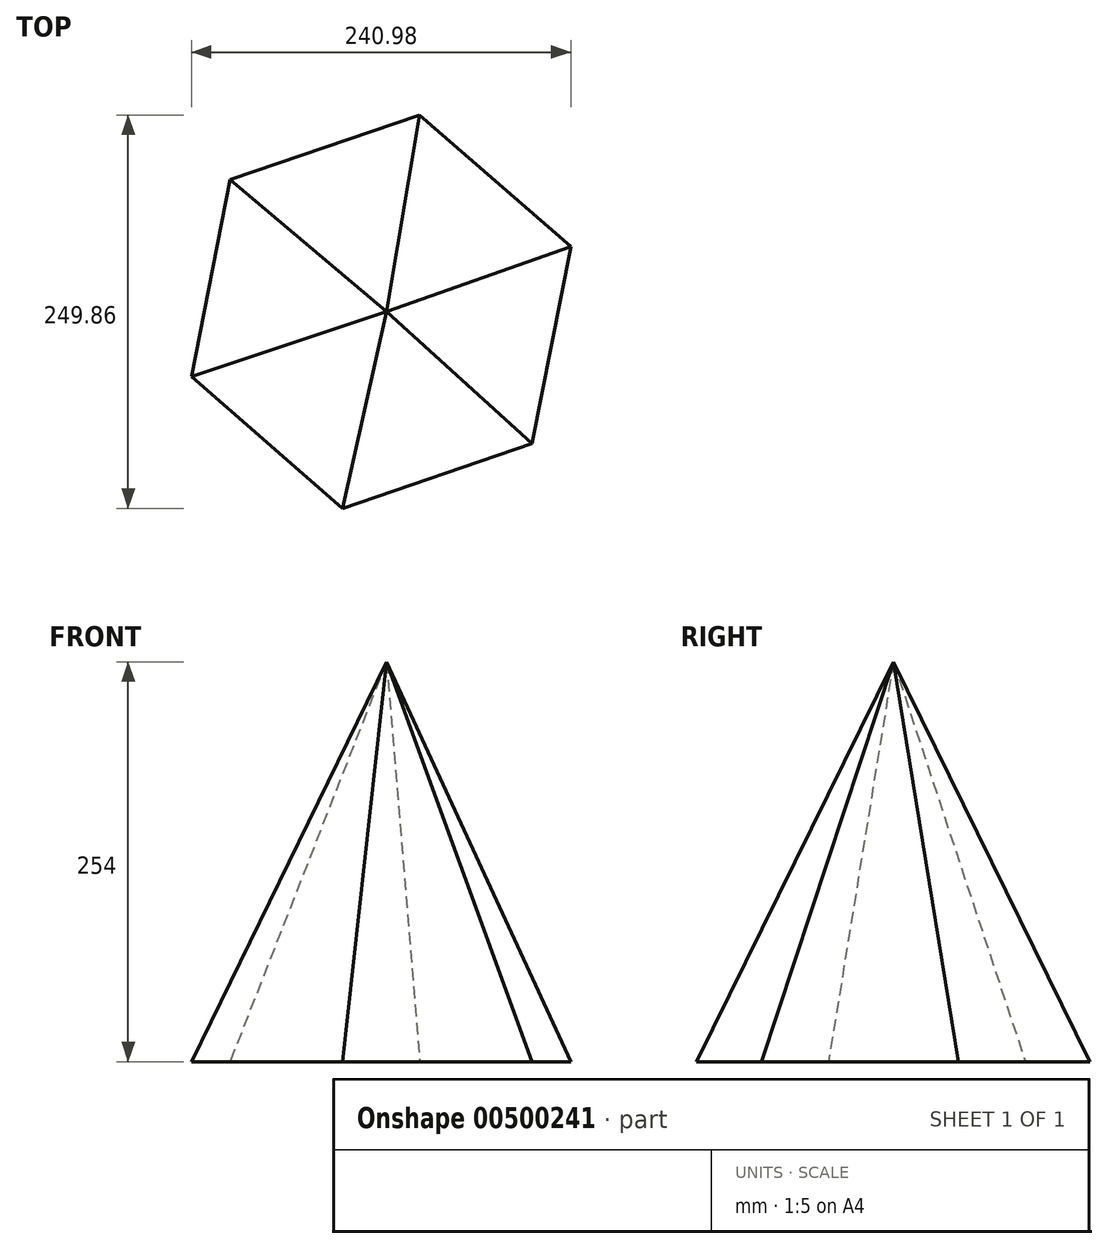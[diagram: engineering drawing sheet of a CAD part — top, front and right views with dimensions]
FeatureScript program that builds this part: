
annotation { "Feature Type Name" : "Feature", "Feature Type Description" : "" }
export const myFeature = defineFeature(function(context is Context, id is Id, definition is map)
    precondition{}
    {
        {
            var Q0;
            Q0=qCreatedBy(makeId("Top.planeOp"),FACE);
            var sketch = newSketch(context, id + "F0", { "sketchPlane" : qUnion([Q0])});
            skCircle(sketch, "E0.cCircle", {"center": v(-3.44, 0) * mm, "radius": 127.33 * mm, "construction": true});
            skLineSegment(sketch, "E0.0", {"start": v(-123.93, -41.17) * mm, "end": v(-99.34, 83.76) * mm});
            skLineSegment(sketch, "E0.1", {"start": v(-99.34, 83.76) * mm, "end": v(21.15, 124.93) * mm});
            skLineSegment(sketch, "E0.2", {"start": v(21.15, 124.93) * mm, "end": v(117.05, 41.17) * mm});
            skLineSegment(sketch, "E0.3", {"start": v(117.05, 41.17) * mm, "end": v(92.46, -83.76) * mm});
            skLineSegment(sketch, "E0.4", {"start": v(92.46, -83.76) * mm, "end": v(-28.04, -124.93) * mm});
            skLineSegment(sketch, "E0.5", {"start": v(-28.04, -124.93) * mm, "end": v(-123.93, -41.17) * mm});
            skSolve(sketch);
        }
        {
            var Q0;
            Q0=qCreatedBy(makeId("Top.planeOp"),FACE);
            cPlane(context, id + "F1", {"entities" : qUnion([Q0]), "cplaneType" : CPlaneType.OFFSET, "offset" : 254 * mm, "width" : 150 * mm, "height" : 150 * mm});
        }
        {
            var Q0;
            Q0=qCreatedBy(id+"F1.planeOp",FACE);
            var sketch = newSketch(context, id + "F2", { "sketchPlane" : qUnion([Q0])});
            skPoint(sketch, "E1", {"position": v(0, 0) * mm});
            skSolve(sketch);
        }
        {
            var Q0;
            Q0=sQuery(id+"F2.wireOp",VERTEX,"E1");
            var Q1;
            Q1=makeQuery(id+"F0.imprint","IMPRINT",FACE,{"disambiguationData":[TD([[makeQuery(id+"F0.imprint","IMPRINT",EDGE,{"derivedFrom":sQuery(id+"F0.wireOp",EDGE,"E0.0")}),-1.0]])]});
            loft(context, id + "F3", {"sheetProfilesArray" : [{ "sheetProfileEntities" : qUnion([Q0]) }, { "sheetProfileEntities" : qUnion([Q1]) }]});
        }
    });
